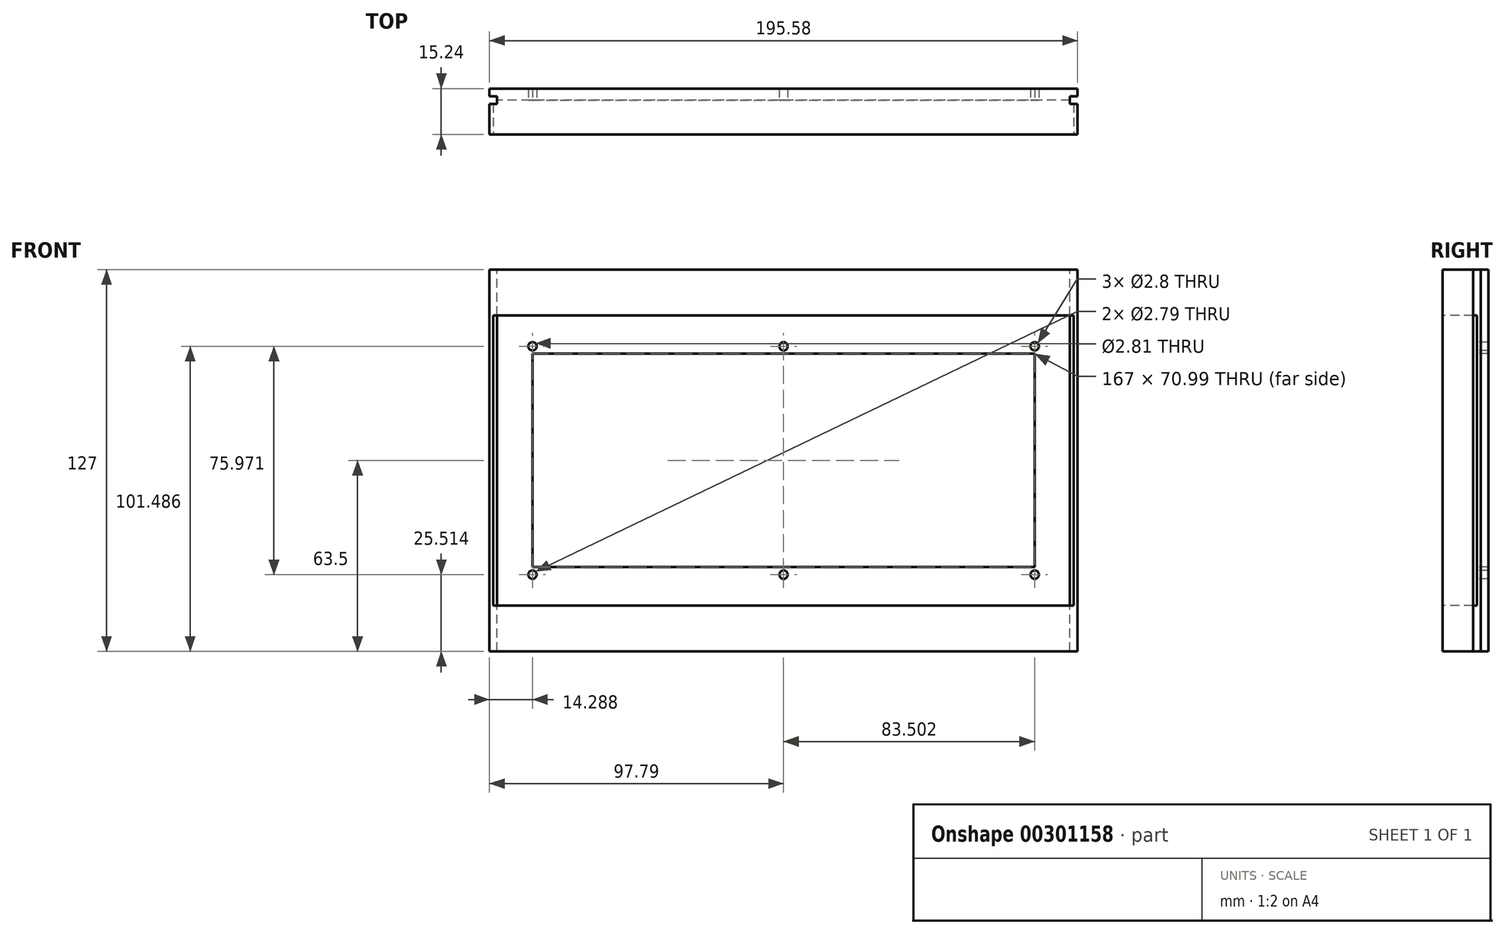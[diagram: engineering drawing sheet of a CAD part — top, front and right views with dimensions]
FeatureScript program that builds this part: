
annotation { "Feature Type Name" : "Feature", "Feature Type Description" : "" }
export const myFeature = defineFeature(function(context is Context, id is Id, definition is map)
    precondition{}
    {
        {
            var Q0;
            Q0=qCreatedBy(makeId("Front.planeOp"),FACE);
            var sketch = newSketch(context, id + "F0", { "sketchPlane" : qUnion([Q0])});
            skLineSegment(sketch, "E0.bottom", {"start": v(97.8, 63.5) * mm, "end": v(-97.8, 63.5) * mm});
            skLineSegment(sketch, "E0.top", {"start": v(97.79, -63.5) * mm, "end": v(-97.8, -63.5) * mm});
            skLineSegment(sketch, "E0.left", {"start": v(97.8, 63.5) * mm, "end": v(97.79, -63.5) * mm});
            skLineSegment(sketch, "E0.right", {"start": v(-97.79, 63.5) * mm, "end": v(-97.8, -63.5) * mm});
            skPoint(sketch, "E0.middle", {"position": v(0, 0) * mm});
            skSolve(sketch);
        }
        {
            var Q0;
            Q0 = qSketchRegion(id + "F0", true);
            extrude(context, id + "F1", {"entities" : qUnion([Q0]), "depth" : 15.24 * mm});
        }
        {
            var Q0;
            Q0=makeQuery(id+"F1.opExtrude","SWEPT_FACE",FACE,{"disambiguationData":[OSD([sQuery(id+"F0.wireOp",EDGE,"E0.bottom")])]});
            var sketch = newSketch(context, id + "F2", { "sketchPlane" : qUnion([Q0])});
            skLineSegment(sketch, "E1.bottom", {"start": v(-97.8, -2.54) * mm, "end": v(-95.25, -2.54) * mm});
            skLineSegment(sketch, "E1.top", {"start": v(-97.8, -5.08) * mm, "end": v(-95.25, -5.08) * mm});
            skLineSegment(sketch, "E1.left", {"start": v(-97.8, -2.54) * mm, "end": v(-97.8, -5.08) * mm});
            skLineSegment(sketch, "E1.right", {"start": v(-95.25, -2.54) * mm, "end": v(-95.25, -5.08) * mm});
            skLineSegment(sketch, "E2.bottom", {"start": v(97.8, -2.54) * mm, "end": v(95.25, -2.54) * mm});
            skLineSegment(sketch, "E2.top", {"start": v(97.8, -5.08) * mm, "end": v(95.25, -5.08) * mm});
            skLineSegment(sketch, "E2.left", {"start": v(97.8, -2.54) * mm, "end": v(97.8, -5.08) * mm});
            skLineSegment(sketch, "E2.right", {"start": v(95.25, -2.54) * mm, "end": v(95.25, -5.08) * mm});
            skSolve(sketch);
        }
        {
            var Q0;
            Q0 = qSketchRegion(id + "F2", true);
            extrude(context, id + "F3", {"entities" : qUnion([Q0]), "operationType" : NewBodyOperationType.REMOVE, "oppositeDirection" : true, "depth" : 127 * mm});
        }
        {
            var Q0;
            Q0=makeQuery(id+"F1.opExtrude","CAP_FACE",FACE,{"disambiguationData":[OSD([sQuery(id+"F0.wireOp",EDGE,"E0.bottom"),sQuery(id+"F0.wireOp",EDGE,"E0.top"),sQuery(id+"F0.wireOp",EDGE,"E0.left"),sQuery(id+"F0.wireOp",EDGE,"E0.right")])],"isStart":false});
            var sketch = newSketch(context, id + "F4", { "sketchPlane" : qUnion([Q0])});
            skLineSegment(sketch, "E3.bottom", {"start": v(83.5, 35.5) * mm, "end": v(-83.5, 35.5) * mm});
            skLineSegment(sketch, "E3.top", {"start": v(83.5, -35.5) * mm, "end": v(-83.5, -35.5) * mm});
            skLineSegment(sketch, "E3.left", {"start": v(83.5, 35.5) * mm, "end": v(83.5, -35.5) * mm});
            skLineSegment(sketch, "E3.right", {"start": v(-83.5, 35.5) * mm, "end": v(-83.5, -35.5) * mm});
            skPoint(sketch, "E3.middle", {"position": v(0, 0) * mm});
            skSolve(sketch);
        }
        {
            var Q0;
            Q0 = qSketchRegion(id + "F4", true);
            extrude(context, id + "F5", {"entities" : qUnion([Q0]), "operationType" : NewBodyOperationType.REMOVE, "oppositeDirection" : true, "depth" : 15.24 * mm});
        }
        {
            var Q0;
            Q0=makeQuery(id+"F1.opExtrude","CAP_FACE",FACE,{"disambiguationData":[OSD([sQuery(id+"F0.wireOp",EDGE,"E0.bottom"),sQuery(id+"F0.wireOp",EDGE,"E0.top"),sQuery(id+"F0.wireOp",EDGE,"E0.left"),sQuery(id+"F0.wireOp",EDGE,"E0.right")])],"isStart":false});
            var sketch = newSketch(context, id + "F6", { "sketchPlane" : qUnion([Q0])});
            skLineSegment(sketch, "E4.bottom", {"start": v(-86.04, 39.81) * mm, "end": v(86.04, 39.81) * mm});
            skLineSegment(sketch, "E4.top", {"start": v(-86.04, -39.81) * mm, "end": v(86.04, -39.81) * mm});
            skLineSegment(sketch, "E4.left", {"start": v(-86.04, 39.81) * mm, "end": v(-86.04, -39.81) * mm});
            skLineSegment(sketch, "E4.right", {"start": v(86.04, 39.81) * mm, "end": v(86.04, -39.81) * mm});
            skSolve(sketch);
        }
        {
            var Q0;
            Q0 = qSketchRegion(id + "F6", true);
            extrude(context, id + "F7", {"entities" : qUnion([Q0]), "operationType" : NewBodyOperationType.REMOVE, "oppositeDirection" : true, "depth" : 11.43 * mm});
        }
        {
            var Q0;
            Q0=makeQuery(id+"F7.boolean.opBoolean","COPY",FACE,{"derivedFrom":makeQuery(id+"F7.opExtrude","CAP_FACE",FACE,{"disambiguationData":[OSD([sQuery(id+"F6.wireOp",EDGE,"E4.bottom"),sQuery(id+"F6.wireOp",EDGE,"E4.top"),sQuery(id+"F6.wireOp",EDGE,"E4.left"),sQuery(id+"F6.wireOp",EDGE,"E4.right")])],"isStart":false})});
            var sketch = newSketch(context, id + "F8", { "sketchPlane" : qUnion([Q0])});
            skCircle(sketch, "E5", {"center": v(0, 37.99) * mm, "radius": 1.4 * mm});
            skCircle(sketch, "E6", {"center": v(-83.5, 37.99) * mm, "radius": 1.4 * mm});
            skCircle(sketch, "E7", {"center": v(-83.5, -37.99) * mm, "radius": 1.4 * mm});
            skCircle(sketch, "E8", {"center": v(0, -37.99) * mm, "radius": 1.4 * mm});
            skCircle(sketch, "E9", {"center": v(83.5, -37.99) * mm, "radius": 1.4 * mm});
            skCircle(sketch, "E10", {"center": v(83.5, 37.99) * mm, "radius": 1.4 * mm});
            skSolve(sketch);
        }
        {
            var Q0;
            Q0 = qSketchRegion(id + "F8", true);
            extrude(context, id + "F9", {"entities" : qUnion([Q0]), "operationType" : NewBodyOperationType.REMOVE, "oppositeDirection" : true, "depth" : 3.8 * mm});
        }
        {
            var Q0;
            Q0=makeQuery(id+"F1.opExtrude","CAP_FACE",FACE,{"disambiguationData":[OSD([sQuery(id+"F0.wireOp",EDGE,"E0.bottom"),sQuery(id+"F0.wireOp",EDGE,"E0.top"),sQuery(id+"F0.wireOp",EDGE,"E0.left"),sQuery(id+"F0.wireOp",EDGE,"E0.right")])],"isStart":false});
            var sketch = newSketch(context, id + "F10", { "sketchPlane" : qUnion([Q0])});
            skLineSegment(sketch, "E11.bottom", {"start": v(96.52, 48.26) * mm, "end": v(-96.52, 48.26) * mm});
            skLineSegment(sketch, "E11.top", {"start": v(96.52, -48.26) * mm, "end": v(-96.52, -48.26) * mm});
            skLineSegment(sketch, "E11.left", {"start": v(96.52, 48.26) * mm, "end": v(96.52, -48.26) * mm});
            skLineSegment(sketch, "E11.right", {"start": v(-96.52, 48.26) * mm, "end": v(-96.52, -48.26) * mm});
            skPoint(sketch, "E11.middle", {"position": v(0, 0) * mm});
            skSolve(sketch);
        }
        {
            var Q0;
            Q0 = qSketchRegion(id + "F10", true);
            extrude(context, id + "F11", {"entities" : qUnion([Q0]), "operationType" : NewBodyOperationType.REMOVE, "oppositeDirection" : true, "depth" : 11.43 * mm});
        }
    });
